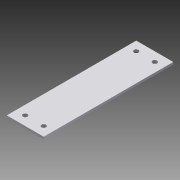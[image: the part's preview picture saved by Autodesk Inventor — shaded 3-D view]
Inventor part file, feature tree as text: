
AUTODESK INVENTOR PART (.ipt)
format: ipt  version: 2015 (Build 190159000, 159)  size: 82,944 bytes
history: native  units: in
note: dims shown in document units (in); Inventor stores cm internally (conversion verified against a paired STEP export)
features: extrude x1, sketch x1
ambient origin geometry x8: Origin, YZ Plane, XZ Plane, XY Plane, X Axis, Y Axis, Z Axis, Center Point
bodies: Solid1 (feature_tree)
feature tree (2):
  extrude  "Extrusion1"  Depth=7.0in
  sketch  "Sketch1"  dims[d0=2.0in d1=7.0in d2=0.125in d3=0.0in d6=0.25in d7=0.5in d8=0.5in]
